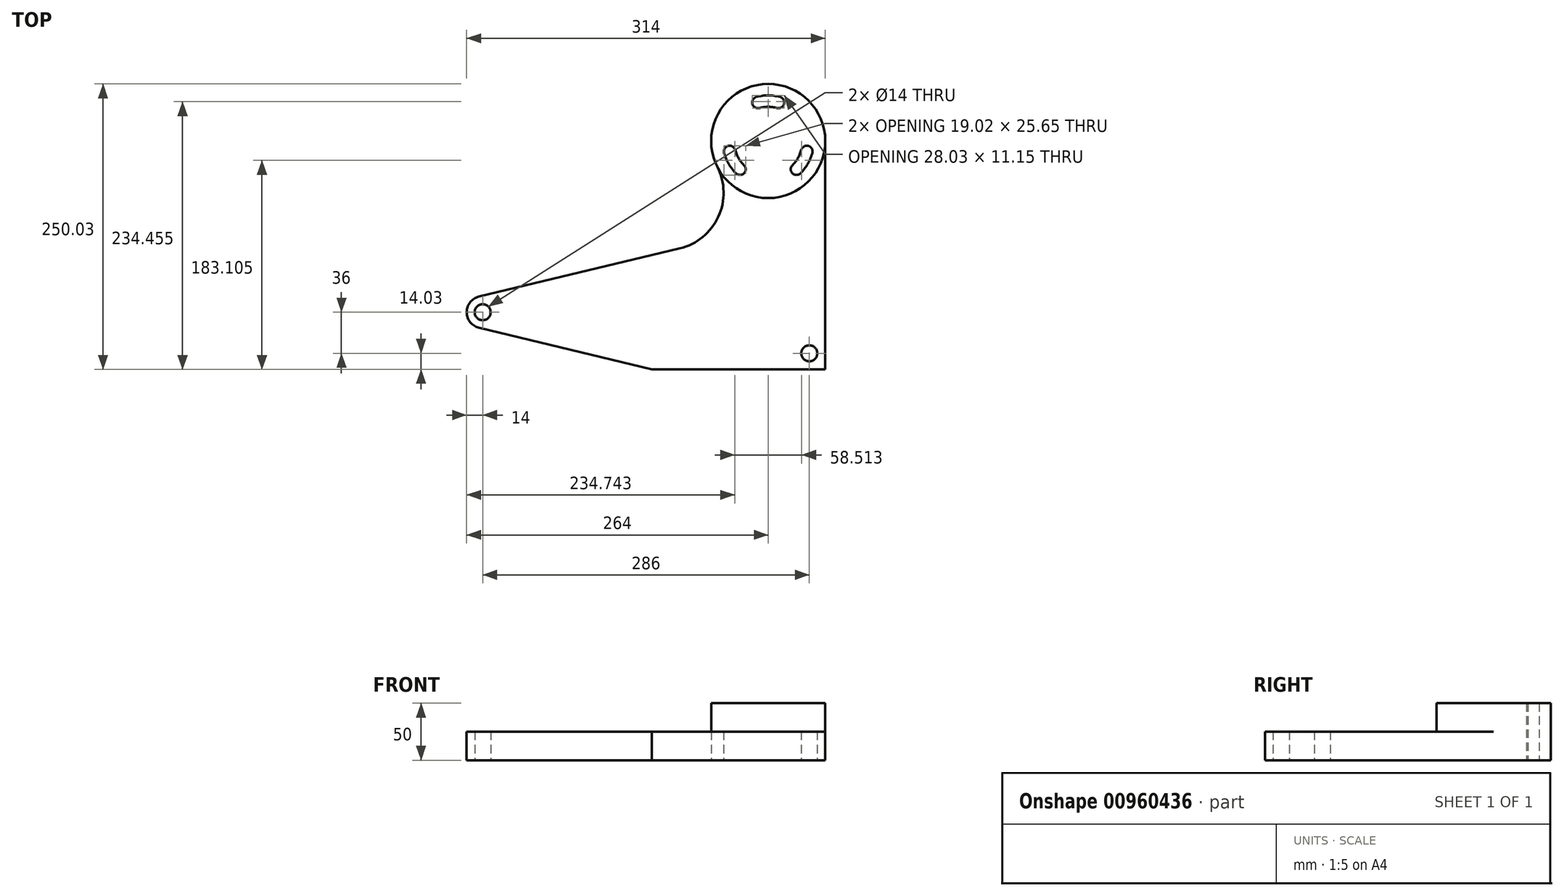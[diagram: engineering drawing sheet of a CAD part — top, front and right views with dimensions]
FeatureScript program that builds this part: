
annotation { "Feature Type Name" : "Feature", "Feature Type Description" : "" }
export const myFeature = defineFeature(function(context is Context, id is Id, definition is map)
    precondition{}
    {
        {
            var Q0;
            Q0=qCreatedBy(makeId("Top.planeOp"),FACE);
            var sketch = newSketch(context, id + "F0", { "sketchPlane" : qUnion([Q0])});
            skLineSegment(sketch, "E0", {"start": v(0, 0) * mm, "end": v(0, 200) * mm});
            skCircle(sketch, "E1", {"center": v(-50, 200) * mm, "radius": 50 * mm});
            skArc(sketch, "E2.0", {"start": v(-50, 240) * mm, "mid": v(-55.22, 239.66) * mm, "end": v(-60.35, 238.64) * mm});
            skArc(sketch, "E3.0", {"start": v(-39.65, 238.64) * mm, "mid": v(-44.78, 239.66) * mm, "end": v(-50, 240) * mm});
            skArc(sketch, "E4.0", {"start": v(-42.24, 228.98) * mm, "mid": v(-50, 230) * mm, "end": v(-57.76, 228.98) * mm});
            skLineSegment(sketch, "E5", {"start": v(-50, 200) * mm, "end": v(-50, 254.57) * mm});
            skArc(sketch, "E6", {"start": v(-42.24, 228.98) * mm, "mid": v(-36.11, 232.51) * mm, "end": v(-39.65, 238.64) * mm});
            skArc(sketch, "E7.MirrorCS", {"start": v(-57.76, 228.98) * mm, "mid": v(-63.89, 232.51) * mm, "end": v(-60.35, 238.64) * mm});
            skArc(sketch, "E8.1.0", {"start": v(-88.64, 189.65) * mm, "mid": v(-86.96, 184.7) * mm, "end": v(-84.64, 180) * mm});
            skArc(sketch, "E8.1.1", {"start": v(-78.98, 192.24) * mm, "mid": v(-85.1, 195.77) * mm, "end": v(-88.64, 189.65) * mm});
            skArc(sketch, "E8.1.2", {"start": v(-78.98, 192.24) * mm, "mid": v(-75.98, 185) * mm, "end": v(-71.21, 178.79) * mm});
            skArc(sketch, "E8.1.3", {"start": v(-71.21, 178.79) * mm, "mid": v(-71.21, 171.72) * mm, "end": v(-78.28, 171.72) * mm});
            skArc(sketch, "E8.1.4", {"start": v(-84.64, 180) * mm, "mid": v(-81.73, 175.65) * mm, "end": v(-78.28, 171.72) * mm});
            skArc(sketch, "E8.2.0", {"start": v(-21.72, 171.72) * mm, "mid": v(-18.27, 175.65) * mm, "end": v(-15.36, 180) * mm});
            skArc(sketch, "E8.2.1", {"start": v(-28.79, 178.79) * mm, "mid": v(-28.79, 171.72) * mm, "end": v(-21.72, 171.72) * mm});
            skArc(sketch, "E8.2.2", {"start": v(-28.79, 178.79) * mm, "mid": v(-24.02, 185) * mm, "end": v(-21.02, 192.24) * mm});
            skArc(sketch, "E8.2.3", {"start": v(-21.02, 192.24) * mm, "mid": v(-14.9, 195.77) * mm, "end": v(-11.36, 189.65) * mm});
            skArc(sketch, "E8.2.4", {"start": v(-15.36, 180) * mm, "mid": v(-13.04, 184.7) * mm, "end": v(-11.36, 189.65) * mm});
            skCircle(sketch, "E9", {"center": v(-300, 50) * mm, "radius": 7 * mm});
            skCircle(sketch, "E10", {"center": v(-300, 50) * mm, "radius": 14 * mm});
            skLineSegment(sketch, "E11", {"start": v(0, 0) * mm, "end": v(-152, -0.03) * mm});
            skLineSegment(sketch, "E12", {"start": v(-152, -0.03) * mm, "end": v(-303.28, 36.39) * mm});
            skLineSegment(sketch, "E13.MirrorCS", {"start": v(-127.38, 105.96) * mm, "end": v(-303.28, 63.61) * mm});
            skArc(sketch, "E14", {"start": v(-127.38, 105.96) * mm, "mid": v(-93.67, 133.66) * mm, "end": v(-94.54, 177.29) * mm});
            skCircle(sketch, "E15", {"center": v(-14, 14) * mm, "radius": 7 * mm});
            skSolve(sketch);
        }
        {
            var Q0;
            {var subQ1=sQuery(id+"F0.wireOp",EDGE,"E0");Q0=makeQuery(id+"F0.imprint","IMPRINT",FACE,{"disambiguationData":[TD([[makeQuery(id+"F0.imprint","IMPRINT",EDGE,{"derivedFrom":subQ1}),1.0]])]});}
            var Q1;
            Q1=makeQuery(id+"F0.imprint","IMPRINT",FACE,{"disambiguationData":[TD([[makeQuery(id+"F0.imprint","IMPRINT",EDGE,{"derivedFrom":sQuery(id+"F0.wireOp",EDGE,"E9")}),-1.0]])]});
            extrude(context, id + "F1", {"entities" : qUnion([Q0, Q1]), "depth" : 25 * mm, "offsetDistance" : 25 * mm});
        }
        {
            var Q0;
            Q0=makeQuery(id+"F0.imprint","IMPRINT",FACE,{"disambiguationData":[TD([[makeQuery(id+"F0.imprint","IMPRINT",EDGE,{"derivedFrom":sQuery(id+"F0.wireOp",EDGE,"E2.0")}),-1.0]])]});
            extrude(context, id + "F2", {"entities" : qUnion([Q0]), "operationType" : NewBodyOperationType.ADD, "depth" : 50 * mm, "offsetDistance" : 25 * mm});
        }
    });
